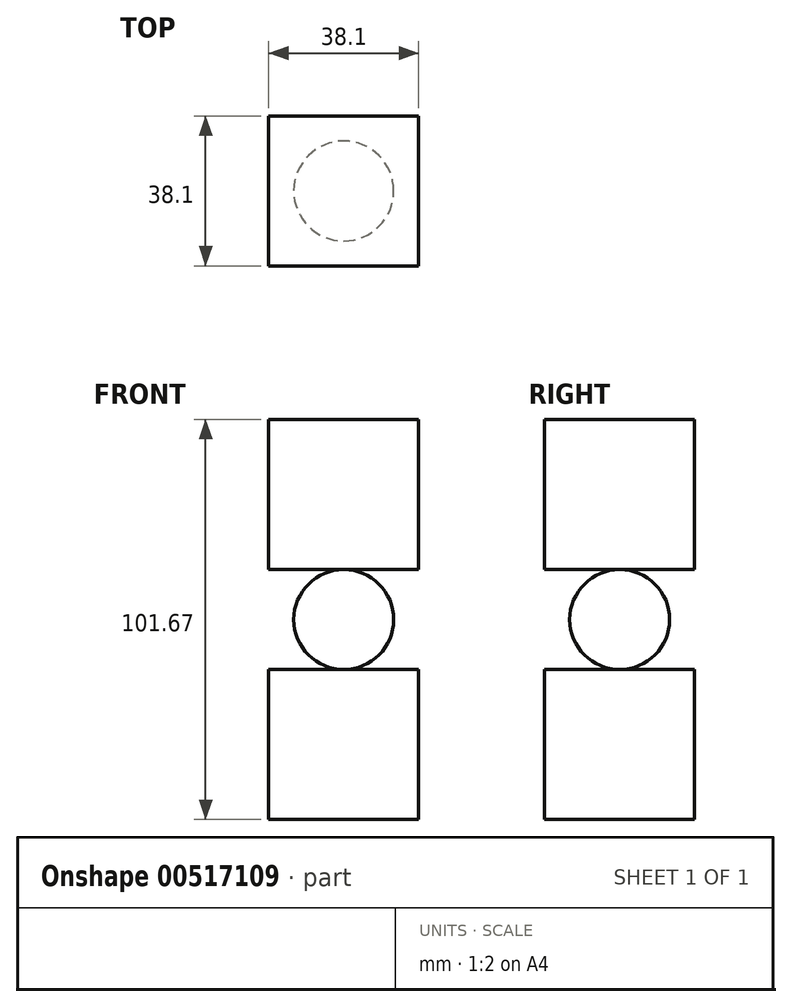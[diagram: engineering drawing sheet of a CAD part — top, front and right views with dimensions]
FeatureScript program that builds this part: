
annotation { "Feature Type Name" : "Feature", "Feature Type Description" : "" }
export const myFeature = defineFeature(function(context is Context, id is Id, definition is map)
    precondition{}
    {
        {
            var Q0;
            Q0=qCreatedBy(makeId("Front.planeOp"),FACE);
            var sketch = newSketch(context, id + "F0", { "sketchPlane" : qUnion([Q0])});
            skLineSegment(sketch, "E0.bottom", {"start": v(-19.05, -31.74) * mm, "end": v(19.05, -31.74) * mm});
            skLineSegment(sketch, "E0.top", {"start": v(-19.05, -69.84) * mm, "end": v(19.05, -69.84) * mm});
            skLineSegment(sketch, "E0.left", {"start": v(-19.05, -31.74) * mm, "end": v(-19.05, -69.84) * mm});
            skLineSegment(sketch, "E0.right", {"start": v(19.05, -31.74) * mm, "end": v(19.05, -69.84) * mm});
            skLineSegment(sketch, "E1", {"start": v(0, -6.34) * mm, "end": v(0, -31.74) * mm});
            skArc(sketch, "E2", {"start": v(0, -31.74) * mm, "mid": v(12.7, -19.04) * mm, "end": v(0, -6.34) * mm});
            skLineSegment(sketch, "E3.bottom", {"start": v(-19.05, 31.83) * mm, "end": v(19.05, 31.83) * mm});
            skLineSegment(sketch, "E3.top", {"start": v(-19.05, -6.27) * mm, "end": v(19.05, -6.27) * mm});
            skLineSegment(sketch, "E3.left", {"start": v(-19.05, 31.83) * mm, "end": v(-19.05, -6.27) * mm});
            skLineSegment(sketch, "E3.right", {"start": v(19.05, 31.83) * mm, "end": v(19.05, -6.27) * mm});
            skLineSegment(sketch, "E4.bottom", {"start": v(19.05, 31.83) * mm, "end": v(44.45, 31.83) * mm});
            skLineSegment(sketch, "E4.top", {"start": v(19.05, 0) * mm, "end": v(44.45, 0) * mm});
            skLineSegment(sketch, "E4.left", {"start": v(19.05, 31.83) * mm, "end": v(19.05, 0) * mm});
            skLineSegment(sketch, "E4.right", {"start": v(44.45, 31.83) * mm, "end": v(44.45, 0) * mm});
            skSolve(sketch);
        }
        {
            var Q0;
            {var subQ0=sQuery(id+"F0.wireOp",EDGE,"E1");Q0=makeQuery(id+"F0.imprint","IMPRINT",FACE,{"disambiguationData":[TD([[makeQuery(id+"F0.imprint","IMPRINT",EDGE,{"derivedFrom":subQ0}),1.0]])]});}
            var Q1;
            Q1=sQuery(id+"F0.wireOp",EDGE,"E1");
            var Q2;
            Q2=sQuery(id+"F0.wireOp",EDGE,"E1");
            revolve(context, id + "F1", {"entities" : qUnion([Q0]), "surfaceEntities" : qUnion([Q1]), "axis" : qUnion([Q2]), "revolveType" : RevolveType.FULL});
        }
        {
            var Q0;
            Q0=makeQuery(id+"F0.imprint","IMPRINT",FACE,{"disambiguationData":[TD([[makeQuery(id+"F0.imprint","IMPRINT",EDGE,{"derivedFrom":sQuery(id+"F0.wireOp",EDGE,"E3.bottom")}),-1.0]])]});
            var Q1;
            Q1=makeQuery(id+"F0.imprint","IMPRINT",FACE,{"disambiguationData":[TD([[makeQuery(id+"F0.imprint","IMPRINT",EDGE,{"derivedFrom":sQuery(id+"F0.wireOp",EDGE,"E0.top")}),1.0]])]});
            extrude(context, id + "F2", {"entities" : qUnion([Q0, Q1]), "depth" : 19.05 * mm, "offsetDistance" : 25.4 * mm});
        }
        {
            var Q0;
            Q0=makeQuery(id+"F2.opExtrude","CAP_FACE",FACE,{"disambiguationData":[OSD([sQuery(id+"F0.wireOp",EDGE,"E3.bottom"),sQuery(id+"F0.wireOp",EDGE,"E3.top"),sQuery(id+"F0.wireOp",EDGE,"E3.left"),sQuery(id+"F0.wireOp",EDGE,"E3.right")])],"isStart":true});
            var Q1;
            Q1=makeQuery(id+"F2.opExtrude","CAP_FACE",FACE,{"disambiguationData":[OSD([sQuery(id+"F0.wireOp",EDGE,"E0.bottom"),sQuery(id+"F0.wireOp",EDGE,"E0.top"),sQuery(id+"F0.wireOp",EDGE,"E0.left"),sQuery(id+"F0.wireOp",EDGE,"E0.right")])],"isStart":true});
            extrude(context, id + "F3", {"entities" : qUnion([Q0, Q1]), "operationType" : NewBodyOperationType.ADD, "depth" : 19.05 * mm, "offsetDistance" : 25.4 * mm});
        }
    });
